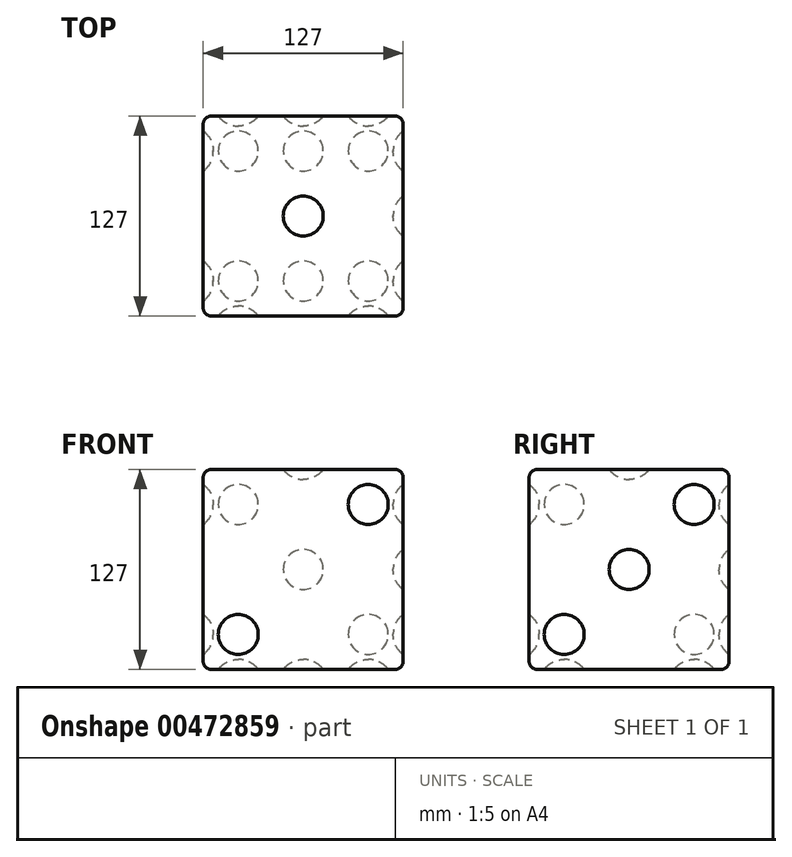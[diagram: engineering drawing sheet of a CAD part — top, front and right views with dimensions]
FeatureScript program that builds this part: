
annotation { "Feature Type Name" : "Feature", "Feature Type Description" : "" }
export const myFeature = defineFeature(function(context is Context, id is Id, definition is map)
    precondition{}
    {
        {
            var Q0;
            Q0=qCreatedBy(makeId("Front.planeOp"),FACE);
            var sketch = newSketch(context, id + "F0", { "sketchPlane" : qUnion([Q0])});
            skLineSegment(sketch, "E0.bottom", {"start": v(0, 0) * mm, "end": v(127, 0) * mm});
            skLineSegment(sketch, "E0.top", {"start": v(0, 127) * mm, "end": v(127, 127) * mm});
            skLineSegment(sketch, "E0.left", {"start": v(0, 0) * mm, "end": v(0, 127) * mm});
            skLineSegment(sketch, "E0.right", {"start": v(127, 0) * mm, "end": v(127, 127) * mm});
            skSolve(sketch);
        }
        {
            var Q0;
            Q0 = qSketchRegion(id + "F0", true);
            extrude(context, id + "F1", {"entities" : qUnion([Q0]), "depth" : 127 * mm});
        }
        {
            var Q0;
            Q0=makeQuery(id+"F1.opExtrude","SWEPT_FACE",FACE,{"disambiguationData":[OSD([sQuery(id+"F0.wireOp",EDGE,"E0.top")])]});
            var sketch = newSketch(context, id + "F2", { "sketchPlane" : qUnion([Q0])});
            skCircle(sketch, "E1", {"center": v(63.5, -63.5) * mm, "radius": 12.7 * mm});
            skPoint(sketch, "E1.centerSnap0", {"position": v(63.5, 0) * mm});
            skPoint(sketch, "E1.centerSnap1", {"position": v(127, -63.5) * mm});
            skSolve(sketch);
        }
        {
            var Q0;
            Q0 = qSketchRegion(id + "F2", true);
            extrude(context, id + "F3", {"entities" : qUnion([Q0]), "operationType" : NewBodyOperationType.REMOVE, "oppositeDirection" : true, "depth" : 6.35 * mm});
        }
        {
            var Q0;
            Q0=makeQuery(id+"F1.opExtrude","CAP_FACE",FACE,{"disambiguationData":[OSD([sQuery(id+"F0.wireOp",EDGE,"E0.bottom"),sQuery(id+"F0.wireOp",EDGE,"E0.top"),sQuery(id+"F0.wireOp",EDGE,"E0.left"),sQuery(id+"F0.wireOp",EDGE,"E0.right")])],"isStart":false});
            var sketch = newSketch(context, id + "F4", { "sketchPlane" : qUnion([Q0])});
            skCircle(sketch, "E2", {"center": v(22.23, 22.23) * mm, "radius": 12.7 * mm});
            skCircle(sketch, "E3", {"center": v(104.77, 104.78) * mm, "radius": 12.7 * mm});
            skSolve(sketch);
        }
        {
            var Q0;
            Q0 = qSketchRegion(id + "F4", true);
            extrude(context, id + "F5", {"entities" : qUnion([Q0]), "operationType" : NewBodyOperationType.REMOVE, "oppositeDirection" : true, "depth" : 6.35 * mm});
        }
        {
            var Q0;
            Q0=makeQuery(id+"F1.opExtrude","SWEPT_FACE",FACE,{"disambiguationData":[OSD([sQuery(id+"F0.wireOp",EDGE,"E0.bottom")])]});
            var sketch = newSketch(context, id + "F6", { "sketchPlane" : qUnion([Q0])});
            skCircle(sketch, "E4", {"center": v(104.78, 104.78) * mm, "radius": 12.7 * mm});
            skCircle(sketch, "E5", {"center": v(104.78, 22.22) * mm, "radius": 12.7 * mm});
            skCircle(sketch, "E6", {"center": v(22.23, 104.78) * mm, "radius": 12.7 * mm});
            skCircle(sketch, "E7", {"center": v(22.23, 22.22) * mm, "radius": 12.7 * mm});
            skCircle(sketch, "E8", {"center": v(63.5, 104.78) * mm, "radius": 12.7 * mm});
            skCircle(sketch, "E9", {"center": v(63.5, 22.22) * mm, "radius": 12.7 * mm});
            skSolve(sketch);
        }
        {
            var Q0;
            Q0 = qSketchRegion(id + "F6", true);
            extrude(context, id + "F7", {"entities" : qUnion([Q0]), "operationType" : NewBodyOperationType.REMOVE, "oppositeDirection" : true, "depth" : 6.35 * mm});
        }
        {
            var Q0;
            Q0=makeQuery(id+"F1.opExtrude","CAP_FACE",FACE,{"disambiguationData":[OSD([sQuery(id+"F0.wireOp",EDGE,"E0.bottom"),sQuery(id+"F0.wireOp",EDGE,"E0.top"),sQuery(id+"F0.wireOp",EDGE,"E0.left"),sQuery(id+"F0.wireOp",EDGE,"E0.right")])],"isStart":true});
            var sketch = newSketch(context, id + "F8", { "sketchPlane" : qUnion([Q0])});
            skCircle(sketch, "E10", {"center": v(-104.77, 104.78) * mm, "radius": 12.7 * mm});
            skCircle(sketch, "E11", {"center": v(-22.23, 104.78) * mm, "radius": 12.7 * mm});
            skCircle(sketch, "E12", {"center": v(-104.78, 22.23) * mm, "radius": 12.7 * mm});
            skCircle(sketch, "E13", {"center": v(-22.23, 22.23) * mm, "radius": 12.7 * mm});
            skCircle(sketch, "E14", {"center": v(-63.5, 63.5) * mm, "radius": 12.7 * mm});
            skPoint(sketch, "E14.centerSnap0", {"position": v(-127, 63.5) * mm});
            skPoint(sketch, "E14.centerSnap1", {"position": v(-63.5, 0) * mm});
            skSolve(sketch);
        }
        {
            var Q0;
            Q0 = qSketchRegion(id + "F8", true);
            extrude(context, id + "F9", {"entities" : qUnion([Q0]), "operationType" : NewBodyOperationType.REMOVE, "oppositeDirection" : true, "depth" : 6.35 * mm});
        }
        {
            var Q0;
            Q0=makeQuery(id+"F1.opExtrude","SWEPT_FACE",FACE,{"disambiguationData":[OSD([sQuery(id+"F0.wireOp",EDGE,"E0.left")])]});
            var sketch = newSketch(context, id + "F10", { "sketchPlane" : qUnion([Q0])});
            skCircle(sketch, "E15", {"center": v(22.23, 22.23) * mm, "radius": 12.7 * mm});
            skCircle(sketch, "E16", {"center": v(22.23, 104.78) * mm, "radius": 12.7 * mm});
            skCircle(sketch, "E17", {"center": v(104.78, 22.23) * mm, "radius": 12.7 * mm});
            skCircle(sketch, "E18", {"center": v(104.78, 104.78) * mm, "radius": 12.7 * mm});
            skSolve(sketch);
        }
        {
            var Q0;
            Q0=makeQuery(id+"F1.opExtrude","SWEPT_FACE",FACE,{"disambiguationData":[OSD([sQuery(id+"F0.wireOp",EDGE,"E0.right")])]});
            var sketch = newSketch(context, id + "F11", { "sketchPlane" : qUnion([Q0])});
            skCircle(sketch, "E19", {"center": v(-22.23, 104.77) * mm, "radius": 12.7 * mm});
            skCircle(sketch, "E20", {"center": v(-104.78, 22.22) * mm, "radius": 12.7 * mm});
            skCircle(sketch, "E21", {"center": v(-63.5, 63.5) * mm, "radius": 12.7 * mm});
            skPoint(sketch, "E21.centerSnap0", {"position": v(-127, 63.5) * mm});
            skPoint(sketch, "E21.centerSnap1", {"position": v(-63.5, 0) * mm});
            skSolve(sketch);
        }
        {
            var Q0;
            Q0 = qSketchRegion(id + "F11", true);
            extrude(context, id + "F12", {"entities" : qUnion([Q0]), "operationType" : NewBodyOperationType.REMOVE, "oppositeDirection" : true, "depth" : 6.35 * mm});
        }
        {
            var Q0;
            Q0 = qSketchRegion(id + "F10", true);
            extrude(context, id + "F13", {"entities" : qUnion([Q0]), "operationType" : NewBodyOperationType.REMOVE, "oppositeDirection" : true, "depth" : 6.35 * mm});
        }
        {
            var Q0;
            Q0=makeQuery(id+"F1.opExtrude","CAP_EDGE",EDGE,{"disambiguationData":[OSD([sQuery(id+"F0.wireOp",EDGE,"E0.right")])],"isStart":false});
            var Q1;
            Q1=makeQuery(id+"F1.opExtrude","SWEPT_EDGE",EDGE,{"disambiguationData":[OSD([sQuery(id+"F0.wireOp",EDGE,"E0.top"),sQuery(id+"F0.wireOp",EDGE,"E0.right")])]});
            var Q2;
            Q2=makeQuery(id+"F1.opExtrude","CAP_EDGE",EDGE,{"disambiguationData":[OSD([sQuery(id+"F0.wireOp",EDGE,"E0.top")])],"isStart":false});
            var Q3;
            Q3=makeQuery(id+"F1.opExtrude","CAP_EDGE",EDGE,{"disambiguationData":[OSD([sQuery(id+"F0.wireOp",EDGE,"E0.left")])],"isStart":false});
            var Q4;
            Q4=makeQuery(id+"F1.opExtrude","SWEPT_EDGE",EDGE,{"disambiguationData":[OSD([sQuery(id+"F0.wireOp",EDGE,"E0.top"),sQuery(id+"F0.wireOp",EDGE,"E0.left")])]});
            var Q5;
            Q5=makeQuery(id+"F1.opExtrude","CAP_EDGE",EDGE,{"disambiguationData":[OSD([sQuery(id+"F0.wireOp",EDGE,"E0.bottom")])],"isStart":false});
            var Q6;
            Q6=makeQuery(id+"F1.opExtrude","SWEPT_EDGE",EDGE,{"disambiguationData":[OSD([sQuery(id+"F0.wireOp",EDGE,"E0.bottom"),sQuery(id+"F0.wireOp",EDGE,"E0.left")])]});
            var Q7;
            Q7=makeQuery(id+"F1.opExtrude","CAP_EDGE",EDGE,{"disambiguationData":[OSD([sQuery(id+"F0.wireOp",EDGE,"E0.bottom")])],"isStart":true});
            var Q8;
            Q8=makeQuery(id+"F1.opExtrude","CAP_EDGE",EDGE,{"disambiguationData":[OSD([sQuery(id+"F0.wireOp",EDGE,"E0.left")])],"isStart":true});
            var Q9;
            Q9=makeQuery(id+"F1.opExtrude","SWEPT_EDGE",EDGE,{"disambiguationData":[OSD([sQuery(id+"F0.wireOp",EDGE,"E0.bottom"),sQuery(id+"F0.wireOp",EDGE,"E0.right")])]});
            var Q10;
            Q10=makeQuery(id+"F1.opExtrude","CAP_EDGE",EDGE,{"disambiguationData":[OSD([sQuery(id+"F0.wireOp",EDGE,"E0.top")])],"isStart":true});
            var Q11;
            Q11=makeQuery(id+"F1.opExtrude","CAP_EDGE",EDGE,{"disambiguationData":[OSD([sQuery(id+"F0.wireOp",EDGE,"E0.right")])],"isStart":true});
            fillet(context, id + "F14", {"entities" : qUnion([Q0, Q1, Q2, Q3, Q4, Q5, Q6, Q7, Q8, Q9, Q10, Q11]), "radius" : 5.08 * mm, "tangentPropagation" : true, "allowEdgeOverflow" : false});
        }
        {
            var Q0;
            Q0=makeQuery(id+"F5.boolean.opBoolean","COPY",FACE,{"derivedFrom":makeQuery(id+"F5.opExtrude","CAP_FACE",FACE,{"disambiguationData":[OSD([sQuery(id+"F4.wireOp",EDGE,"E3")])],"isStart":false})});
            var Q1;
            Q1=makeQuery(id+"F5.boolean.opBoolean","COPY",FACE,{"derivedFrom":makeQuery(id+"F5.opExtrude","CAP_FACE",FACE,{"disambiguationData":[OSD([sQuery(id+"F4.wireOp",EDGE,"E2")])],"isStart":false})});
            var Q2;
            Q2=makeQuery(id+"F12.boolean.opBoolean","COPY",FACE,{"derivedFrom":makeQuery(id+"F12.opExtrude","CAP_FACE",FACE,{"disambiguationData":[OSD([sQuery(id+"F11.wireOp",EDGE,"E20")])],"isStart":false})});
            var Q3;
            Q3=makeQuery(id+"F12.boolean.opBoolean","COPY",FACE,{"derivedFrom":makeQuery(id+"F12.opExtrude","CAP_FACE",FACE,{"disambiguationData":[OSD([sQuery(id+"F11.wireOp",EDGE,"E21")])],"isStart":false})});
            var Q4;
            Q4=makeQuery(id+"F12.boolean.opBoolean","COPY",FACE,{"derivedFrom":makeQuery(id+"F12.opExtrude","CAP_FACE",FACE,{"disambiguationData":[OSD([sQuery(id+"F11.wireOp",EDGE,"E19")])],"isStart":false})});
            var Q5;
            Q5=makeQuery(id+"F3.boolean.opBoolean","COPY",FACE,{"derivedFrom":makeQuery(id+"F3.opExtrude","CAP_FACE",FACE,{"disambiguationData":[OSD([sQuery(id+"F2.wireOp",EDGE,"E1")])],"isStart":false})});
            var Q6;
            Q6=makeQuery(id+"F9.boolean.opBoolean","COPY",FACE,{"derivedFrom":makeQuery(id+"F9.opExtrude","CAP_FACE",FACE,{"disambiguationData":[OSD([sQuery(id+"F8.wireOp",EDGE,"E10")])],"isStart":false})});
            var Q7;
            Q7=makeQuery(id+"F9.boolean.opBoolean","COPY",FACE,{"derivedFrom":makeQuery(id+"F9.opExtrude","CAP_FACE",FACE,{"disambiguationData":[OSD([sQuery(id+"F8.wireOp",EDGE,"E11")])],"isStart":false})});
            var Q8;
            Q8=makeQuery(id+"F9.boolean.opBoolean","COPY",FACE,{"derivedFrom":makeQuery(id+"F9.opExtrude","CAP_FACE",FACE,{"disambiguationData":[OSD([sQuery(id+"F8.wireOp",EDGE,"E14")])],"isStart":false})});
            var Q9;
            Q9=makeQuery(id+"F9.boolean.opBoolean","COPY",FACE,{"derivedFrom":makeQuery(id+"F9.opExtrude","CAP_FACE",FACE,{"disambiguationData":[OSD([sQuery(id+"F8.wireOp",EDGE,"E12")])],"isStart":false})});
            var Q10;
            Q10=makeQuery(id+"F9.boolean.opBoolean","COPY",FACE,{"derivedFrom":makeQuery(id+"F9.opExtrude","CAP_FACE",FACE,{"disambiguationData":[OSD([sQuery(id+"F8.wireOp",EDGE,"E13")])],"isStart":false})});
            var Q11;
            Q11=makeQuery(id+"F13.boolean.opBoolean","COPY",FACE,{"derivedFrom":makeQuery(id+"F13.opExtrude","CAP_FACE",FACE,{"disambiguationData":[OSD([sQuery(id+"F10.wireOp",EDGE,"E16")])],"isStart":false})});
            var Q12;
            Q12=makeQuery(id+"F13.boolean.opBoolean","COPY",FACE,{"derivedFrom":makeQuery(id+"F13.opExtrude","CAP_FACE",FACE,{"disambiguationData":[OSD([sQuery(id+"F10.wireOp",EDGE,"E18")])],"isStart":false})});
            var Q13;
            Q13=makeQuery(id+"F13.boolean.opBoolean","COPY",FACE,{"derivedFrom":makeQuery(id+"F13.opExtrude","CAP_FACE",FACE,{"disambiguationData":[OSD([sQuery(id+"F10.wireOp",EDGE,"E17")])],"isStart":false})});
            var Q14;
            Q14=makeQuery(id+"F13.boolean.opBoolean","COPY",FACE,{"derivedFrom":makeQuery(id+"F13.opExtrude","CAP_FACE",FACE,{"disambiguationData":[OSD([sQuery(id+"F10.wireOp",EDGE,"E15")])],"isStart":false})});
            var Q15;
            Q15=makeQuery(id+"F7.boolean.opBoolean","COPY",FACE,{"derivedFrom":makeQuery(id+"F7.opExtrude","CAP_FACE",FACE,{"disambiguationData":[OSD([sQuery(id+"F6.wireOp",EDGE,"E6")])],"isStart":false})});
            var Q16;
            Q16=makeQuery(id+"F7.boolean.opBoolean","COPY",FACE,{"derivedFrom":makeQuery(id+"F7.opExtrude","CAP_FACE",FACE,{"disambiguationData":[OSD([sQuery(id+"F6.wireOp",EDGE,"E8")])],"isStart":false})});
            var Q17;
            Q17=makeQuery(id+"F7.boolean.opBoolean","COPY",FACE,{"derivedFrom":makeQuery(id+"F7.opExtrude","CAP_FACE",FACE,{"disambiguationData":[OSD([sQuery(id+"F6.wireOp",EDGE,"E4")])],"isStart":false})});
            var Q18;
            Q18=makeQuery(id+"F7.boolean.opBoolean","COPY",FACE,{"derivedFrom":makeQuery(id+"F7.opExtrude","CAP_FACE",FACE,{"disambiguationData":[OSD([sQuery(id+"F6.wireOp",EDGE,"E5")])],"isStart":false})});
            var Q19;
            Q19=makeQuery(id+"F7.boolean.opBoolean","COPY",FACE,{"derivedFrom":makeQuery(id+"F7.opExtrude","CAP_FACE",FACE,{"disambiguationData":[OSD([sQuery(id+"F6.wireOp",EDGE,"E9")])],"isStart":false})});
            var Q20;
            Q20=makeQuery(id+"F7.boolean.opBoolean","COPY",FACE,{"derivedFrom":makeQuery(id+"F7.opExtrude","CAP_FACE",FACE,{"disambiguationData":[OSD([sQuery(id+"F6.wireOp",EDGE,"E7")])],"isStart":false})});
            fillet(context, id + "F15", {"entities" : qUnion([Q0, Q1, Q2, Q3, Q4, Q5, Q6, Q7, Q8, Q9, Q10, Q11, Q12, Q13, Q14, Q15, Q16, Q17, Q18, Q19, Q20]), "radius" : 15.5 * mm, "tangentPropagation" : true, "allowEdgeOverflow" : false});
        }
    });
